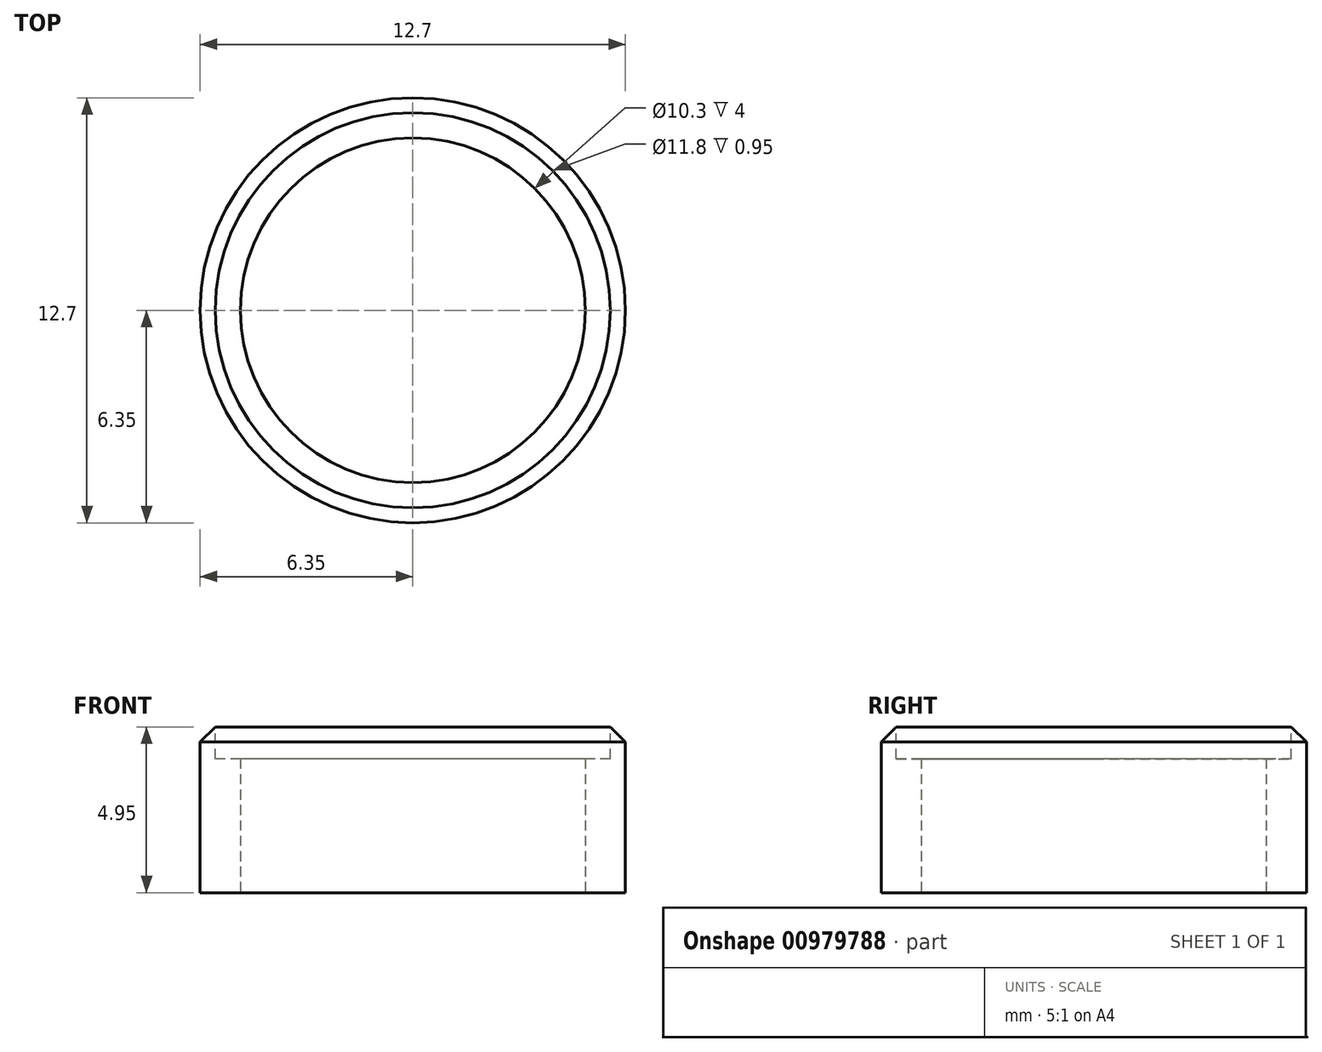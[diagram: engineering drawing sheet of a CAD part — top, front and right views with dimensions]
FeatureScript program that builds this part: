
annotation { "Feature Type Name" : "Feature", "Feature Type Description" : "" }
export const myFeature = defineFeature(function(context is Context, id is Id, definition is map)
    precondition{}
    {
        {
            var Q0;
            Q0=qCreatedBy(makeId("Top.planeOp"),FACE);
            var sketch = newSketch(context, id + "F0", { "sketchPlane" : qUnion([Q0])});
            skCircle(sketch, "E0", {"center": v(0, 0) * mm, "radius": 5.15 * mm});
            skCircle(sketch, "E1", {"center": v(0, 0) * mm, "radius": 6.35 * mm});
            skSolve(sketch);
        }
        {
            var Q0;
            Q0=makeQuery(id+"F0.imprint","IMPRINT",FACE,{"disambiguationData":[TD([[makeQuery(id+"F0.imprint","IMPRINT",EDGE,{"derivedFrom":sQuery(id+"F0.wireOp",EDGE,"E0")}),-1.0]])]});
            extrude(context, id + "F1", {"entities" : qUnion([Q0]), "depth" : 5 * mm, "offsetDistance" : 25 * mm});
        }
        {
            var Q0;
            Q0=makeQuery(id+"F1.opExtrude","CAP_FACE",FACE,{"disambiguationData":[OSD([sQuery(id+"F0.wireOp",EDGE,"E0"),sQuery(id+"F0.wireOp",EDGE,"E1")])],"isStart":false});
            var sketch = newSketch(context, id + "F2", { "sketchPlane" : qUnion([Q0])});
            skCircle(sketch, "E2", {"center": v(0, 0) * mm, "radius": 5.9 * mm});
            skSolve(sketch);
        }
        {
            var Q0;
            Q0=makeQuery(id+"F2.imprint","IMPRINT",FACE,{"disambiguationData":[TD([[makeQuery(id+"F2.imprint","IMPRINT",EDGE,{"derivedFrom":sQuery(id+"F2.wireOp",EDGE,"E2")}),1.0]])]});
            extrude(context, id + "F3", {"entities" : qUnion([Q0]), "operationType" : NewBodyOperationType.REMOVE, "oppositeDirection" : true, "depth" : 1 * mm, "offsetDistance" : 25 * mm});
        }
        {
            var Q0;
            Q0=makeQuery(id+"F1.opExtrude","CAP_EDGE",EDGE,{"disambiguationData":[OSD([sQuery(id+"F0.wireOp",EDGE,"E1")])],"isStart":false});
            chamfer(context, id + "F4", {"entities" : qUnion([Q0]), "width" : 0.5 * mm, "tangentPropagation" : true});
        }
    });
